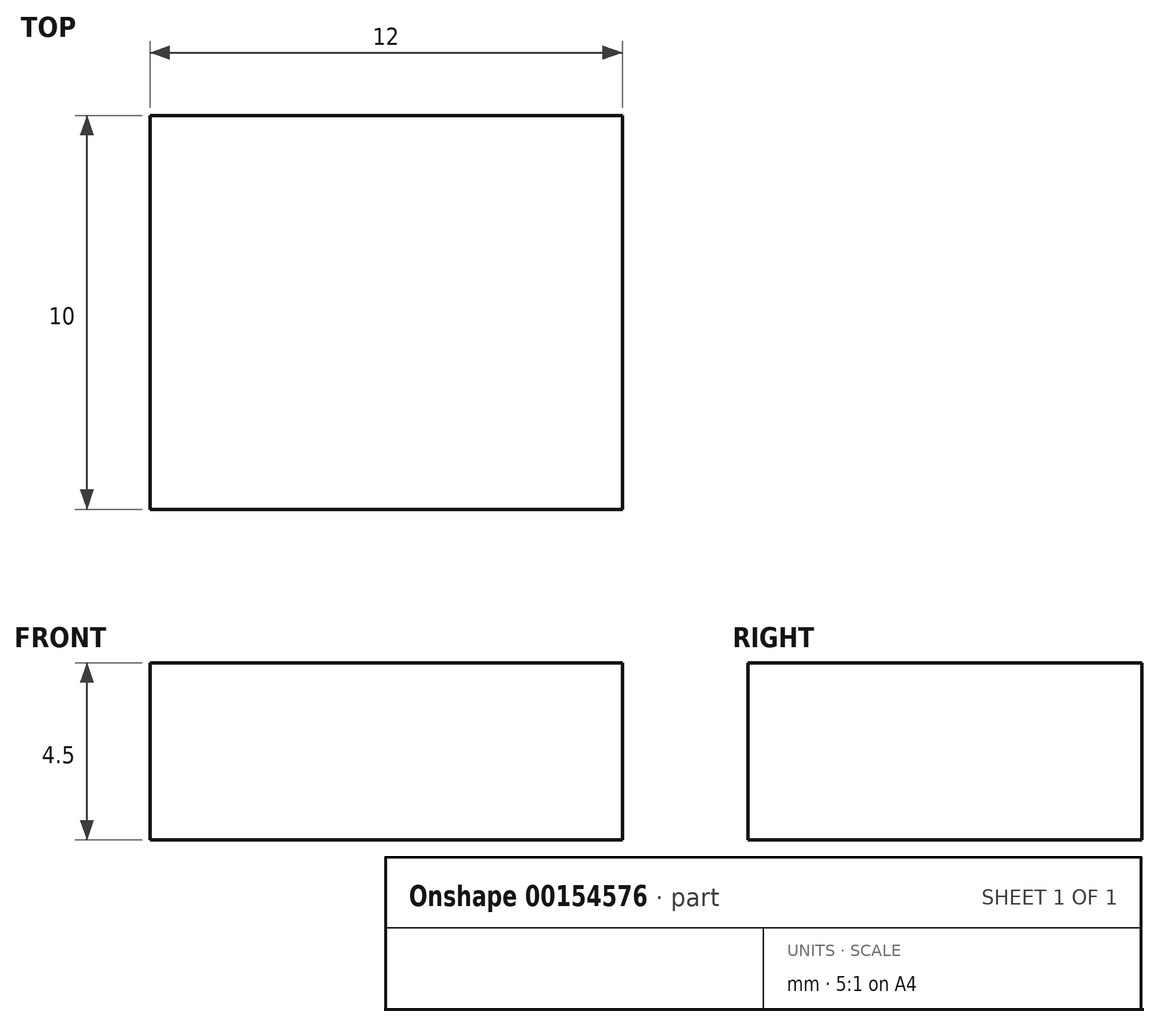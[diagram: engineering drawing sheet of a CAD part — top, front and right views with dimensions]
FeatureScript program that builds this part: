
annotation { "Feature Type Name" : "Feature", "Feature Type Description" : "" }
export const myFeature = defineFeature(function(context is Context, id is Id, definition is map)
    precondition{}
    {
        {
            var Q0;
            Q0=qCreatedBy(makeId("Top.planeOp"),FACE);
            var sketch = newSketch(context, id + "F0", { "sketchPlane" : qUnion([Q0])});
            skLineSegment(sketch, "E0.bottom", {"start": v(6, -5) * mm, "end": v(-6, -5) * mm});
            skLineSegment(sketch, "E0.top", {"start": v(6, 5) * mm, "end": v(-6, 5) * mm});
            skLineSegment(sketch, "E0.left", {"start": v(6, -5) * mm, "end": v(6, 5) * mm});
            skLineSegment(sketch, "E0.right", {"start": v(-6, -5) * mm, "end": v(-6, 5) * mm});
            skPoint(sketch, "E0.middle", {"position": v(0, 0) * mm});
            skSolve(sketch);
        }
        {
            var Q0;
            Q0 = qSketchRegion(id + "F0", true);
            extrude(context, id + "F1", {"entities" : qUnion([Q0]), "depth" : 4.5 * mm});
        }
    });
